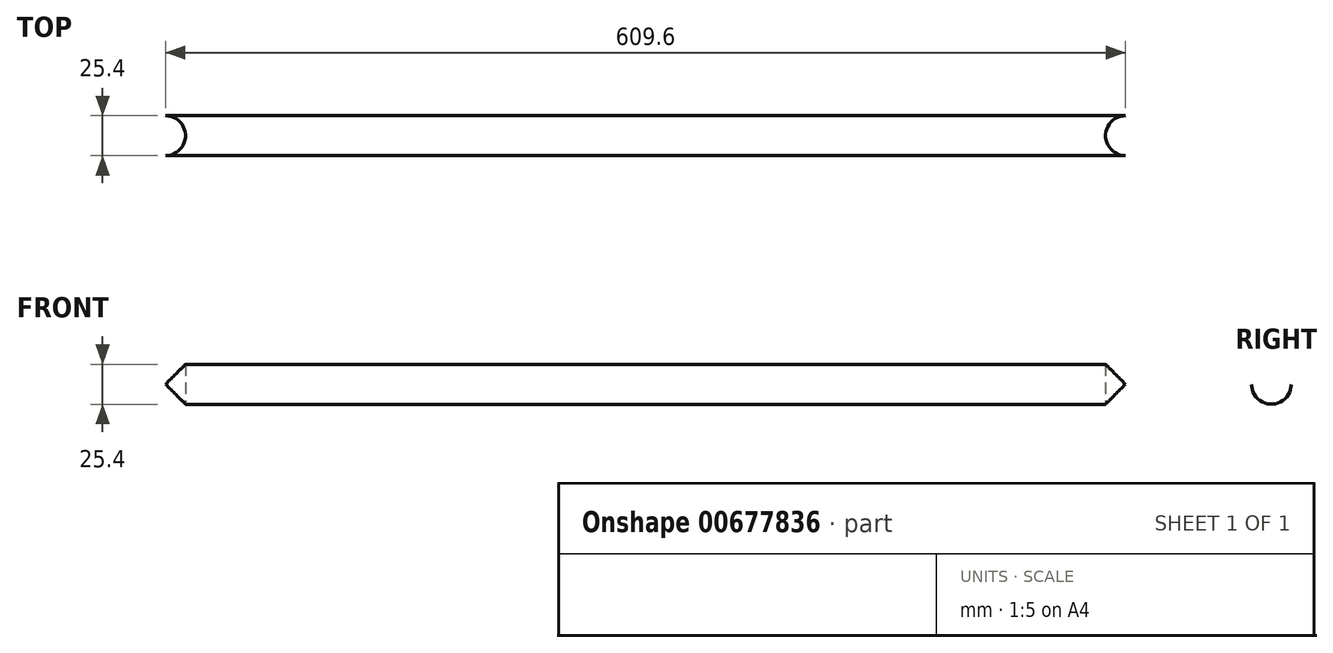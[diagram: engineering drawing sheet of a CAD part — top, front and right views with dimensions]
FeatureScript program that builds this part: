
annotation { "Feature Type Name" : "Feature", "Feature Type Description" : "" }
export const myFeature = defineFeature(function(context is Context, id is Id, definition is map)
    precondition{}
    {
        {
            var Q0;
            Q0=qCreatedBy(makeId("Right.planeOp"),FACE);
            var sketch = newSketch(context, id + "F0", { "sketchPlane" : qUnion([Q0])});
            skCircle(sketch, "E0", {"center": v(0, 0) * mm, "radius": 12.7 * mm});
            skSolve(sketch);
        }
        {
            var Q0;
            Q0 = qSketchRegion(id + "F0", true);
            extrude(context, id + "F1", {"entities" : qUnion([Q0]), "depth" : 609.6 * mm, "offsetDistance" : 25.4 * mm});
        }
        {
            var Q0;
            Q0=qCreatedBy(makeId("Top.planeOp"),FACE);
            var sketch = newSketch(context, id + "F2", { "sketchPlane" : qUnion([Q0])});
            skCircle(sketch, "E1", {"center": v(0, 0) * mm, "radius": 12.7 * mm});
            skCircle(sketch, "E2", {"center": v(609.6, 0) * mm, "radius": 12.7 * mm});
            skSolve(sketch);
        }
        {
            var Q0;
            Q0=makeQuery(id+"F2.imprint","IMPRINT",FACE,{"disambiguationData":[TD([[makeQuery(id+"F2.imprint","IMPRINT",EDGE,{"derivedFrom":sQuery(id+"F2.wireOp",EDGE,"E2")}),1.0]])]});
            var Q1;
            Q1=makeQuery(id+"F2.imprint","IMPRINT",FACE,{"disambiguationData":[TD([[makeQuery(id+"F2.imprint","IMPRINT",EDGE,{"derivedFrom":sQuery(id+"F2.wireOp",EDGE,"E1")}),1.0]])]});
            extrude(context, id + "F3", {"entities" : qUnion([Q0, Q1]), "operationType" : NewBodyOperationType.REMOVE, "endBound" : BoundingType.THROUGH_ALL, "depth" : 25.4 * mm, "offsetDistance" : 25.4 * mm, "hasSecondDirection" : true, "secondDirectionBound" : SecondDirectionBoundingType.THROUGH_ALL, "secondDirectionOppositeDirection" : true, "secondDirectionDepth" : 25.4 * mm});
        }
    });
